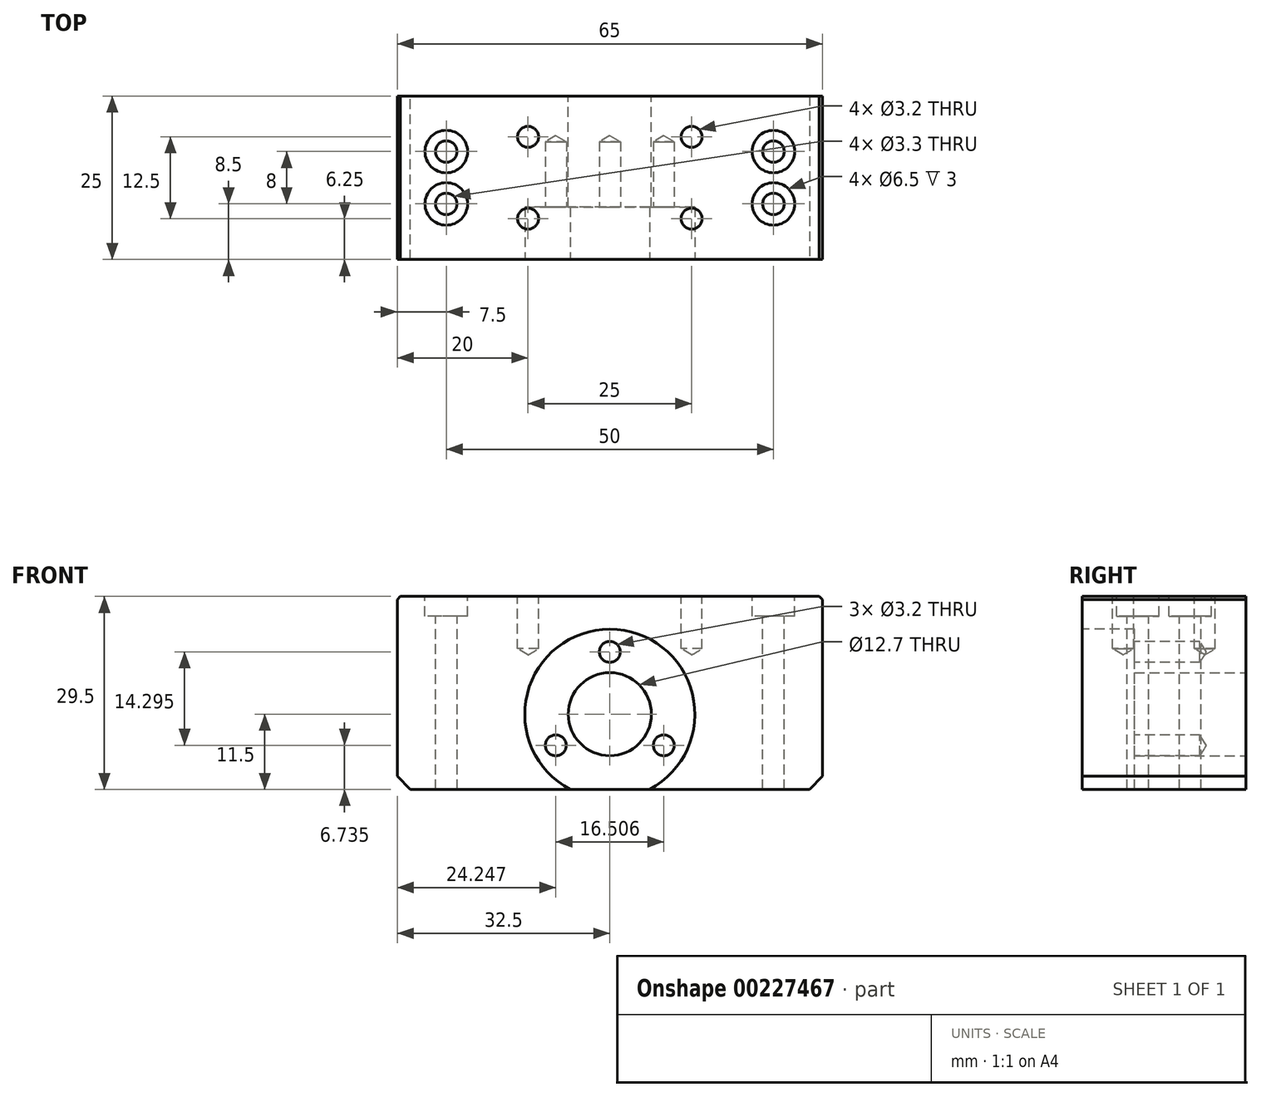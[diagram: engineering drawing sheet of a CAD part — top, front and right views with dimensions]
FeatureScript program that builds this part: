
annotation { "Feature Type Name" : "Feature", "Feature Type Description" : "" }
export const myFeature = defineFeature(function(context is Context, id is Id, definition is map)
    precondition{}
    {
        {
            var Q0;
            Q0=qCreatedBy(makeId("Front.planeOp"),FACE);
            var sketch = newSketch(context, id + "F0", { "sketchPlane" : qUnion([Q0])});
            skLineSegment(sketch, "E0.bottom", {"start": v(32.5, -11.5) * mm, "end": v(-32.5, -11.5) * mm});
            skLineSegment(sketch, "E0.top", {"start": v(32.5, 18) * mm, "end": v(-32.5, 18) * mm});
            skLineSegment(sketch, "E0.left", {"start": v(32.5, -11.5) * mm, "end": v(32.5, 18) * mm});
            skLineSegment(sketch, "E0.right", {"start": v(-32.5, -11.5) * mm, "end": v(-32.5, 18) * mm});
            skPoint(sketch, "E0.middle", {"position": v(0, 0) * mm});
            skCircle(sketch, "E1", {"center": v(0, 0) * mm, "radius": 6.35 * mm});
            skPoint(sketch, "E2", {"position": v(0, -11.5) * mm});
            skPoint(sketch, "E3", {"position": v(32.5, -7.5) * mm});
            skSolve(sketch);
        }
        {
            var Q0;
            {var subQ1=sQuery(id+"F0.wireOp",EDGE,"E0.top");Q0=makeQuery(id+"F0.imprint","IMPRINT",FACE,{"disambiguationData":[TD([[makeQuery(id+"F0.imprint","IMPRINT",EDGE,{"derivedFrom":subQ1}),1.0]])]});}
            extrude(context, id + "F1", {"entities" : qUnion([Q0]), "depth" : 25 * mm});
        }
        {
            var Q0;
            Q0=makeQuery(id+"F1.opExtrude","SWEPT_EDGE",EDGE,{"disambiguationData":[OSD([sQuery(id+"F0.wireOp",EDGE,"E0.top"),sQuery(id+"F0.wireOp",EDGE,"E0.right")])]});
            var Q1;
            Q1=makeQuery(id+"F1.opExtrude","SWEPT_EDGE",EDGE,{"disambiguationData":[OSD([sQuery(id+"F0.wireOp",EDGE,"E0.top"),sQuery(id+"F0.wireOp",EDGE,"E0.left")])]});
            chamfer(context, id + "F2", {"entities" : qUnion([Q0, Q1]), "width" : 0.5 * mm, "tangentPropagation" : true});
        }
        {
            var Q0;
            Q0=makeQuery(id+"F1.opExtrude","CAP_FACE",FACE,{"disambiguationData":[OSD([sQuery(id+"F0.wireOp",EDGE,"E0.bottom"),sQuery(id+"F0.wireOp",EDGE,"E0.top"),sQuery(id+"F0.wireOp",EDGE,"E0.left"),sQuery(id+"F0.wireOp",EDGE,"E0.right"),sQuery(id+"F0.wireOp",EDGE,"E1")])],"isStart":false});
            var sketch = newSketch(context, id + "F3", { "sketchPlane" : qUnion([Q0])});
            skCircle(sketch, "E4", {"center": v(0, 0) * mm, "radius": 13 * mm});
            skSolve(sketch);
        }
        {
            var Q0;
            Q0=makeQuery(id+"F3.imprint","IMPRINT",FACE,{"disambiguationData":[TD([[makeQuery(id+"F3.imprint","IMPRINT",EDGE,{"derivedFrom":makeQuery(id+"F1.opExtrude","CAP_EDGE",EDGE,{"disambiguationData":[OSD([sQuery(id+"F0.wireOp",EDGE,"E1")])],"isStart":false})}),-1.0]])]});
            extrude(context, id + "F4", {"entities" : qUnion([Q0]), "operationType" : NewBodyOperationType.REMOVE, "oppositeDirection" : true, "depth" : 8 * mm});
        }
        {
            var Q0;
            Q0=makeQuery(id+"F1.opExtrude","SWEPT_EDGE",EDGE,{"disambiguationData":[OSD([sQuery(id+"F0.wireOp",EDGE,"E0.bottom"),sQuery(id+"F0.wireOp",EDGE,"E0.left")])]});
            var Q1;
            Q1=makeQuery(id+"F1.opExtrude","SWEPT_EDGE",EDGE,{"disambiguationData":[OSD([sQuery(id+"F0.wireOp",EDGE,"E0.bottom"),sQuery(id+"F0.wireOp",EDGE,"E0.right")])]});
            chamfer(context, id + "F5", {"entities" : qUnion([Q0, Q1]), "width" : 2 * mm, "tangentPropagation" : true});
        }
        {
            var Q0;
            Q0=makeQuery(id+"F1.opExtrude","SWEPT_FACE",FACE,{"disambiguationData":[OSD([sQuery(id+"F0.wireOp",EDGE,"E0.top")])]});
            var sketch = newSketch(context, id + "F6", { "sketchPlane" : qUnion([Q0])});
            skPoint(sketch, "E5", {"position": v(12.5, -6.25) * mm});
            skPoint(sketch, "E6.0.1.0", {"position": v(12.5, -18.75) * mm});
            skPoint(sketch, "E6.1.0.0", {"position": v(-12.5, -6.25) * mm});
            skPoint(sketch, "E6.1.1.0", {"position": v(-12.5, -18.75) * mm});
            skLineSegment(sketch, "E6.direction1", {"start": v(12.5, -6.25) * mm, "end": v(-12.5, -6.25) * mm, "construction": true});
            skLineSegment(sketch, "E6.direction2", {"start": v(12.5, -6.25) * mm, "end": v(12.5, -18.75) * mm, "construction": true});
            skSolve(sketch);
        }
        {
            var Q0;
            Q0=sQuery(id+"F6.wireOp",VERTEX,"E5");
            var Q1;
            Q1=sQuery(id+"F6.wireOp",VERTEX,"E6.0.1.0");
            var Q2;
            Q2=sQuery(id+"F6.wireOp",VERTEX,"E6.1.0.0");
            var Q3;
            Q3=sQuery(id+"F6.wireOp",VERTEX,"E6.1.1.0");
            var Q4;
            Q4=makeQuery(id+"F1.opExtrude","SWEPT_BODY",BODY,{"disambiguationData":[OSD([sQuery(id+"F0.wireOp",EDGE,"E0.bottom"),sQuery(id+"F0.wireOp",EDGE,"E0.top"),sQuery(id+"F0.wireOp",EDGE,"E0.left"),sQuery(id+"F0.wireOp",EDGE,"E0.right"),sQuery(id+"F0.wireOp",EDGE,"E1")])]});
            hole(context, id + "F7", {"style" : HoleStyle.SIMPLE, "endStyle" : HoleEndStyle.BLIND, "standardTappedOrClearance" : lookupTablePath({ "standard" : "ISO", "engagement" : "75%", "pitch" : "0.75 mm", "size" : "M4", "type" : "Tapped" }), "standardBlindInLast" : lookupTablePath({ "standard" : "ISO", "engagement" : "75%", "pitch" : "0.75 mm", "size" : "M4", "type" : "Tapped" }), "holeDiameter" : 3.2 * mm, "holeDepth" : 8 * mm, "locations" : qUnion([Q0, Q1, Q2, Q3]), "scope" : qUnion([Q4])});
        }
        {
            var Q0;
            Q0=makeQuery(id+"F1.opExtrude","SWEPT_FACE",FACE,{"disambiguationData":[OSD([sQuery(id+"F0.wireOp",EDGE,"E0.top")])]});
            var sketch = newSketch(context, id + "F8", { "sketchPlane" : qUnion([Q0])});
            skPoint(sketch, "E7", {"position": v(-25, -8.5) * mm});
            skPoint(sketch, "E8.0.1.0", {"position": v(-25, -16.5) * mm});
            skPoint(sketch, "E8.1.0.0", {"position": v(25, -8.5) * mm});
            skPoint(sketch, "E8.1.1.0", {"position": v(25, -16.5) * mm});
            skLineSegment(sketch, "E8.direction1", {"start": v(-25, -8.5) * mm, "end": v(25, -8.5) * mm, "construction": true});
            skLineSegment(sketch, "E8.direction2", {"start": v(-25, -8.5) * mm, "end": v(-25, -16.5) * mm, "construction": true});
            skSolve(sketch);
        }
        {
            var Q0;
            Q0=sQuery(id+"F8.wireOp",VERTEX,"E7");
            var Q1;
            Q1=sQuery(id+"F8.wireOp",VERTEX,"E8.0.1.0");
            var Q2;
            Q2=sQuery(id+"F8.wireOp",VERTEX,"E8.1.0.0");
            var Q3;
            Q3=sQuery(id+"F8.wireOp",VERTEX,"E8.1.1.0");
            var Q4;
            Q4=makeQuery(id+"F1.opExtrude","SWEPT_BODY",BODY,{"disambiguationData":[OSD([sQuery(id+"F0.wireOp",EDGE,"E0.bottom"),sQuery(id+"F0.wireOp",EDGE,"E0.top"),sQuery(id+"F0.wireOp",EDGE,"E0.left"),sQuery(id+"F0.wireOp",EDGE,"E0.right"),sQuery(id+"F0.wireOp",EDGE,"E1")])]});
            hole(context, id + "F9", {"style" : HoleStyle.C_BORE, "endStyle" : HoleEndStyle.THROUGH, "standardTappedOrClearance" : lookupTablePath({ "standard" : "ISO", "fit" : "Normal", "size" : "M3", "type" : "Clearance" }), "standardBlindInLast" : lookupTablePath({ "fit" : "Standard", "standard" : "ISO", "size" : "M3", "type" : "Clearance" }), "holeDiameter" : 3.3 * mm, "cBoreDiameter" : 6.5 * mm, "cBoreDepth" : 3 * mm, "locations" : qUnion([Q0, Q1, Q2, Q3]), "scope" : qUnion([Q4]), "tappedDepth" : 12 * mm, "tapClearance" : 3});
        }
        {
            var Q0;
            Q0=makeQuery(id+"F4.boolean.opBoolean","COPY",FACE,{"derivedFrom":makeQuery(id+"F4.opExtrude","CAP_FACE",FACE,{"disambiguationData":[OSD([sQuery(id+"F0.wireOp",EDGE,"E0.bottom"),sQuery(id+"F0.wireOp",EDGE,"E1"),sQuery(id+"F3.wireOp",EDGE,"E4")])],"isStart":false})});
            var sketch = newSketch(context, id + "F10", { "sketchPlane" : qUnion([Q0])});
            skCircle(sketch, "E9", {"center": v(0, 0) * mm, "radius": 9.53 * mm, "construction": true});
            skPoint(sketch, "E10", {"position": v(0, 9.53) * mm});
            skPoint(sketch, "E11.1.0", {"position": v(-8.25, -4.76) * mm});
            skPoint(sketch, "E11.2.0", {"position": v(8.25, -4.77) * mm});
            skSolve(sketch);
        }
        {
            var Q0;
            Q0=sQuery(id+"F10.wireOp",VERTEX,"E10");
            var Q1;
            Q1=sQuery(id+"F10.wireOp",VERTEX,"E11.2.0");
            var Q2;
            Q2=sQuery(id+"F10.wireOp",VERTEX,"E11.1.0");
            var Q3;
            Q3=makeQuery(id+"F1.opExtrude","SWEPT_BODY",BODY,{"disambiguationData":[OSD([sQuery(id+"F0.wireOp",EDGE,"E0.bottom"),sQuery(id+"F0.wireOp",EDGE,"E0.top"),sQuery(id+"F0.wireOp",EDGE,"E0.left"),sQuery(id+"F0.wireOp",EDGE,"E0.right"),sQuery(id+"F0.wireOp",EDGE,"E1")])]});
            hole(context, id + "F11", {"style" : HoleStyle.SIMPLE, "endStyle" : HoleEndStyle.BLIND, "standardTappedOrClearance" : lookupTablePath({ "standard" : "ISO", "engagement" : "75%", "pitch" : "0.75 mm", "size" : "M4", "type" : "Tapped" }), "standardBlindInLast" : lookupTablePath({ "standard" : "ISO", "engagement" : "75%", "pitch" : "0.75 mm", "size" : "M4", "type" : "Tapped" }), "holeDiameter" : 3.2 * mm, "holeDepth" : 10 * mm, "locations" : qUnion([Q0, Q1, Q2]), "scope" : qUnion([Q3])});
        }
    });
